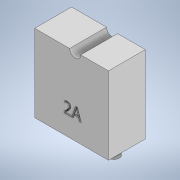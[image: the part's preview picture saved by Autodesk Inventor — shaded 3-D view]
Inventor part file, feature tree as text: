
AUTODESK INVENTOR PART (.ipt)
format: ipt  version: 2021 (Build 250183000, 183)  size: 170,496 bytes
history: native  units: mm
features: sketch x5, extrude x4, emboss x1
ambient origin geometry x8: Origin, YZ Plane, XZ Plane, XY Plane, X Axis, Y Axis, Z Axis, Center Point
bodies: Solid1 (feature_tree)
feature tree (10):
  extrude  "Extrusion1"  Depth=11.4385mm
  extrude  "Extrusion2"  Depth=10.0mm
  emboss  "Emboss1"
  extrude  "Extrusion4"  Depth=20.0mm
  extrude  "Extrusion5"  Depth=3.0mm TaperAngle=0.0deg
  sketch  "Sketch1"  dims[d0=22.877mm d1=11.4385mm]
  sketch  "Sketch2"  dims[d3=10.0mm d4=5.0mm]
  sketch  "Sketch4"  dims[d5=20.0mm d6=0.0mm d7=3.0mm]
  sketch  "Sketch5"  dims[d8=3.5mm d9=3.0mm d10=0.0mm]
  sketch  "Sketch6"  dims[d15=1.0mm d16=0.0mm d18=1.877mm d19=0.0mm d20=3.0mm d21=9.0mm d22=1.877mm d23=0.0mm]
